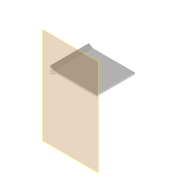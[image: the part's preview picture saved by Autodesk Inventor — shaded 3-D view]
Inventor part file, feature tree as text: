
AUTODESK INVENTOR PART (.ipt)
format: ipt  version: 2022 (Build 260153000, 153)  size: 94,208 bytes
history: native  units: mm
features: reference x5, plane x2, other x2, sketch x1, extrude x1
ambient origin geometry x8: Origin, YZ Plane, XZ Plane, XY Plane, X Axis, Y Axis, Z Axis, Center Point
bodies: Volumenkörper1 (feature_tree)
feature tree (11):
  plane  "Arbeitsebene1"
  sketch  "Skizze1"  dims[d0=0.2mm d1=10.0mm d2=0.0mm d3=0.5mm d4=1.404145mm]
  plane  "Arbeitsebene2"
  extrude  "Extrusion1"  Depth=0.5mm TaperAngle=0.0deg
  reference  "Referenz1"
  reference  "Referenz2"
  reference  "Referenz3"
  reference  "Referenz4"
  reference  "Referenz5"
  other  "Assembly_Matchboxscope_injectionmolded.iam"
  other  "IM_ledmatrix_holder:1"
